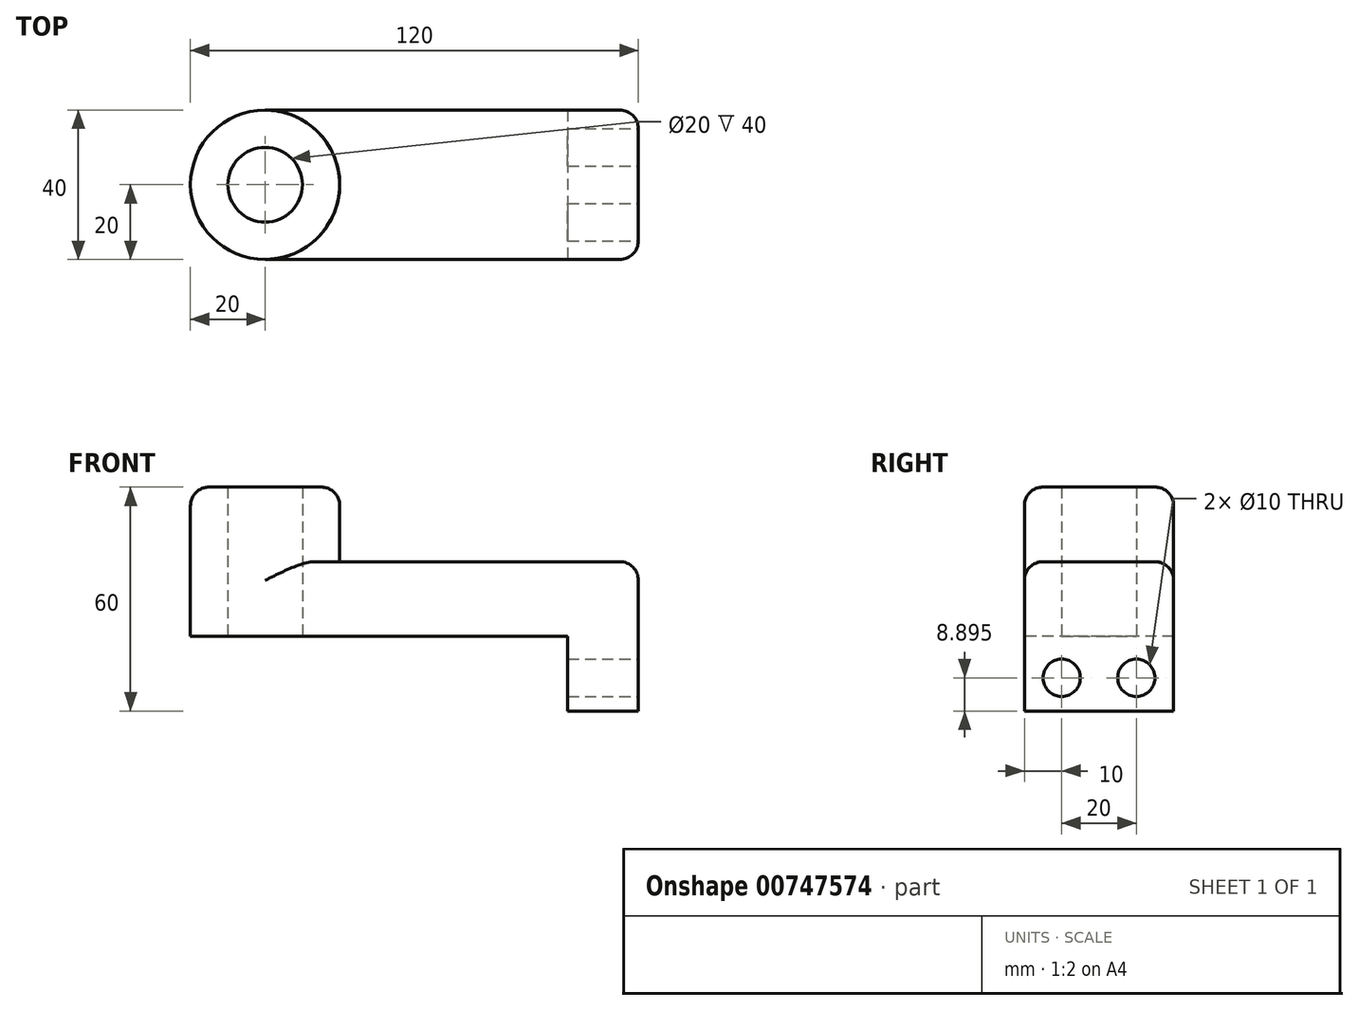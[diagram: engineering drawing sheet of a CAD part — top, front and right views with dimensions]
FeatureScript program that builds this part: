
annotation { "Feature Type Name" : "Feature", "Feature Type Description" : "" }
export const myFeature = defineFeature(function(context is Context, id is Id, definition is map)
    precondition{}
    {
        {
            var Q0;
            Q0=qCreatedBy(makeId("Top.planeOp"),FACE);
            var sketch = newSketch(context, id + "F0", { "sketchPlane" : qUnion([Q0])});
            skCircle(sketch, "E0", {"center": v(0, 0) * mm, "radius": 20 * mm});
            skCircle(sketch, "E1", {"center": v(0, 0) * mm, "radius": 10 * mm});
            skLineSegment(sketch, "E2", {"start": v(0, 20) * mm, "end": v(100, 20) * mm});
            skLineSegment(sketch, "E3", {"start": v(0, -20) * mm, "end": v(100, -20) * mm});
            skLineSegment(sketch, "E4", {"start": v(100, 20) * mm, "end": v(100, -20) * mm});
            skLineSegment(sketch, "E5", {"start": v(81.1, 20) * mm, "end": v(81.1, -20) * mm});
            skSolve(sketch);
        }
        {
            var Q0;
            Q0=makeQuery(id+"F0.imprint","IMPRINT",FACE,{"disambiguationData":[TD([[makeQuery(id+"F0.imprint","IMPRINT",EDGE,{"derivedFrom":sQuery(id+"F0.wireOp",EDGE,"E1")}),-1.0]])]});
            extrude(context, id + "F1", {"entities" : qUnion([Q0]), "depth" : 40 * mm, "offsetDistance" : 25 * mm});
        }
        {
            var Q0;
            {var subQ5=sQuery(id+"F0.wireOp",EDGE,"E5");Q0=makeQuery(id+"F0.imprint","IMPRINT",FACE,{"disambiguationData":[TD([[makeQuery(id+"F0.imprint","IMPRINT",EDGE,{"derivedFrom":subQ5}),-1.0]])]});}
            var sketch = newSketch(context, id + "F2", { "sketchPlane" : qUnion([Q0])});
            skSolve(sketch);
        }
        {
            var Q0;
            {var subQ5=sQuery(id+"F0.wireOp",EDGE,"E5");Q0=makeQuery(id+"F2.imprint","IMPRINT",FACE,{"disambiguationData":[TD([[makeQuery(id+"F2.imprint","IMPRINT",EDGE,{"derivedFrom":makeQuery(id+"F0.imprint","IMPRINT",EDGE,{"derivedFrom":subQ5})}),-1.0]])]});}
            extrude(context, id + "F3", {"entities" : qUnion([Q0]), "operationType" : NewBodyOperationType.ADD, "depth" : 20 * mm, "offsetDistance" : 25 * mm});
        }
        {
            var Q0;
            {var subQ0=sQuery(id+"F0.wireOp",EDGE,"E4");Q0=makeQuery(id+"F0.imprint","IMPRINT",FACE,{"disambiguationData":[TD([[makeQuery(id+"F0.imprint","IMPRINT",EDGE,{"derivedFrom":subQ0}),-1.0]])]});}
            extrude(context, id + "F4", {"entities" : qUnion([Q0]), "operationType" : NewBodyOperationType.ADD, "depth" : 20 * mm, "offsetDistance" : 25 * mm});
        }
        {
            var Q0;
            {var subQ0=sQuery(id+"F0.wireOp",EDGE,"E4");Q0=makeQuery(id+"F0.imprint","IMPRINT",FACE,{"disambiguationData":[TD([[makeQuery(id+"F0.imprint","IMPRINT",EDGE,{"derivedFrom":subQ0}),-1.0]])]});}
            extrude(context, id + "F5", {"entities" : qUnion([Q0]), "operationType" : NewBodyOperationType.ADD, "oppositeDirection" : true, "depth" : 20 * mm, "offsetDistance" : 25 * mm});
        }
        {
            var Q0;
            {var subQ0=sQuery(id+"F0.wireOp",EDGE,"E4");Q0=makeQuery(id+"F5.boolean.opBoolean","MERGE",FACE,{"derivedFrom":[makeQuery(id+"F4.opExtrude","SWEPT_FACE",FACE,{"disambiguationData":[OSD([subQ0])]}),makeQuery(id+"F5.opExtrude","SWEPT_FACE",FACE,{"disambiguationData":[OSD([subQ0])]})]});}
            var sketch = newSketch(context, id + "F6", { "sketchPlane" : qUnion([Q0])});
            skCircle(sketch, "E6", {"center": v(-10, -11.1) * mm, "radius": 5 * mm});
            skCircle(sketch, "E7", {"center": v(10, -11.1) * mm, "radius": 5 * mm});
            skSolve(sketch);
        }
        {
            var Q0;
            Q0=makeQuery(id+"F6.imprint","IMPRINT",FACE,{"disambiguationData":[TD([[makeQuery(id+"F6.imprint","IMPRINT",EDGE,{"derivedFrom":sQuery(id+"F6.wireOp",EDGE,"E6")}),1.0]])]});
            var Q1;
            Q1=sQuery(id+"F6.wireOp",EDGE,"E6");
            extrude(context, id + "F7", {"entities" : qUnion([Q0]), "operationType" : NewBodyOperationType.REMOVE, "surfaceEntities" : qUnion([Q1]), "endBound" : BoundingType.UP_TO_NEXT, "oppositeDirection" : true, "depth" : 25 * mm, "offsetDistance" : 25 * mm});
        }
        {
            var Q0;
            Q0=makeQuery(id+"F6.imprint","IMPRINT",FACE,{"disambiguationData":[TD([[makeQuery(id+"F6.imprint","IMPRINT",EDGE,{"derivedFrom":sQuery(id+"F6.wireOp",EDGE,"E7")}),1.0]])]});
            extrude(context, id + "F8", {"entities" : qUnion([Q0]), "operationType" : NewBodyOperationType.REMOVE, "endBound" : BoundingType.UP_TO_NEXT, "oppositeDirection" : true, "depth" : 25 * mm, "offsetDistance" : 25 * mm});
        }
        {
            var Q0;
            Q0=makeQuery(id+"F1.opExtrude","CAP_EDGE",EDGE,{"disambiguationData":[OSD([sQuery(id+"F0.wireOp",EDGE,"E0")])],"isStart":false});
            var Q1;
            {var subQ0=sQuery(id+"F0.wireOp",EDGE,"E3");Q1=makeQuery(id+"F4.boolean.opBoolean","MERGE",EDGE,{"derivedFrom":[makeQuery(id+"F3.opExtrude","CAP_EDGE",EDGE,{"disambiguationData":[OSD([subQ0])],"isStart":false}),makeQuery(id+"F4.opExtrude","CAP_EDGE",EDGE,{"disambiguationData":[OSD([subQ0])],"isStart":false})]});}
            var Q2;
            {var subQ0=sQuery(id+"F0.wireOp",EDGE,"E2");Q2=makeQuery(id+"F4.boolean.opBoolean","MERGE",EDGE,{"derivedFrom":[makeQuery(id+"F3.opExtrude","CAP_EDGE",EDGE,{"disambiguationData":[OSD([subQ0])],"isStart":false}),makeQuery(id+"F4.opExtrude","CAP_EDGE",EDGE,{"disambiguationData":[OSD([subQ0])],"isStart":false})]});}
            var Q3;
            Q3=makeQuery(id+"F3.opExtrude","CAP_EDGE",EDGE,{"disambiguationData":[OSD([sQuery(id+"F0.wireOp",EDGE,"E0")])],"isStart":false});
            var Q4;
            Q4=makeQuery(id+"F4.opExtrude","CAP_EDGE",EDGE,{"disambiguationData":[OSD([sQuery(id+"F0.wireOp",EDGE,"E4")])],"isStart":false});
            var Q5;
            {var subQ0=sQuery(id+"F0.wireOp",EDGE,"E4");var subQ1=sQuery(id+"F0.wireOp",EDGE,"E2");Q5=makeQuery(id+"F5.boolean.opBoolean","MERGE",EDGE,{"derivedFrom":[makeQuery(id+"F4.opExtrude","SWEPT_EDGE",EDGE,{"disambiguationData":[OSD([subQ1,subQ0])]}),makeQuery(id+"F5.opExtrude","SWEPT_EDGE",EDGE,{"disambiguationData":[OSD([subQ1,subQ0])]})]});}
            var Q6;
            {var subQ0=sQuery(id+"F0.wireOp",EDGE,"E4");var subQ1=sQuery(id+"F0.wireOp",EDGE,"E3");Q6=makeQuery(id+"F5.boolean.opBoolean","MERGE",EDGE,{"derivedFrom":[makeQuery(id+"F4.opExtrude","SWEPT_EDGE",EDGE,{"disambiguationData":[OSD([subQ1,subQ0])]}),makeQuery(id+"F5.opExtrude","SWEPT_EDGE",EDGE,{"disambiguationData":[OSD([subQ1,subQ0])]})]});}
            fillet(context, id + "F9", {"entities" : qUnion([Q0, Q1, Q2, Q3, Q4, Q5, Q6]), "radius" : 5 * mm, "tangentPropagation" : true, "allowEdgeOverflow" : false});
        }
    });
